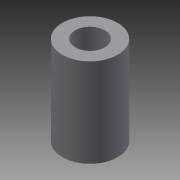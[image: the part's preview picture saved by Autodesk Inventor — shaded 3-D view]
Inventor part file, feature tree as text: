
AUTODESK INVENTOR PART (.ipt)
format: ipt  version: 2013 (Build 170138000, 138)  size: 70,656 bytes
history: native  units: mm
features: extrude x1, sketch x1
ambient origin geometry x8: Origin, YZ Plane, XZ Plane, XY Plane, X Axis, Y Axis, Z Axis, Center Point
bodies: Solid1 (feature_tree)
feature tree (2):
  extrude  "Extrusion1"  Depth=15.0mm
  sketch  "Sketch1"  dims[d0=8.0mm d2=15.0mm d3=24.0mm d4=0.0mm]
